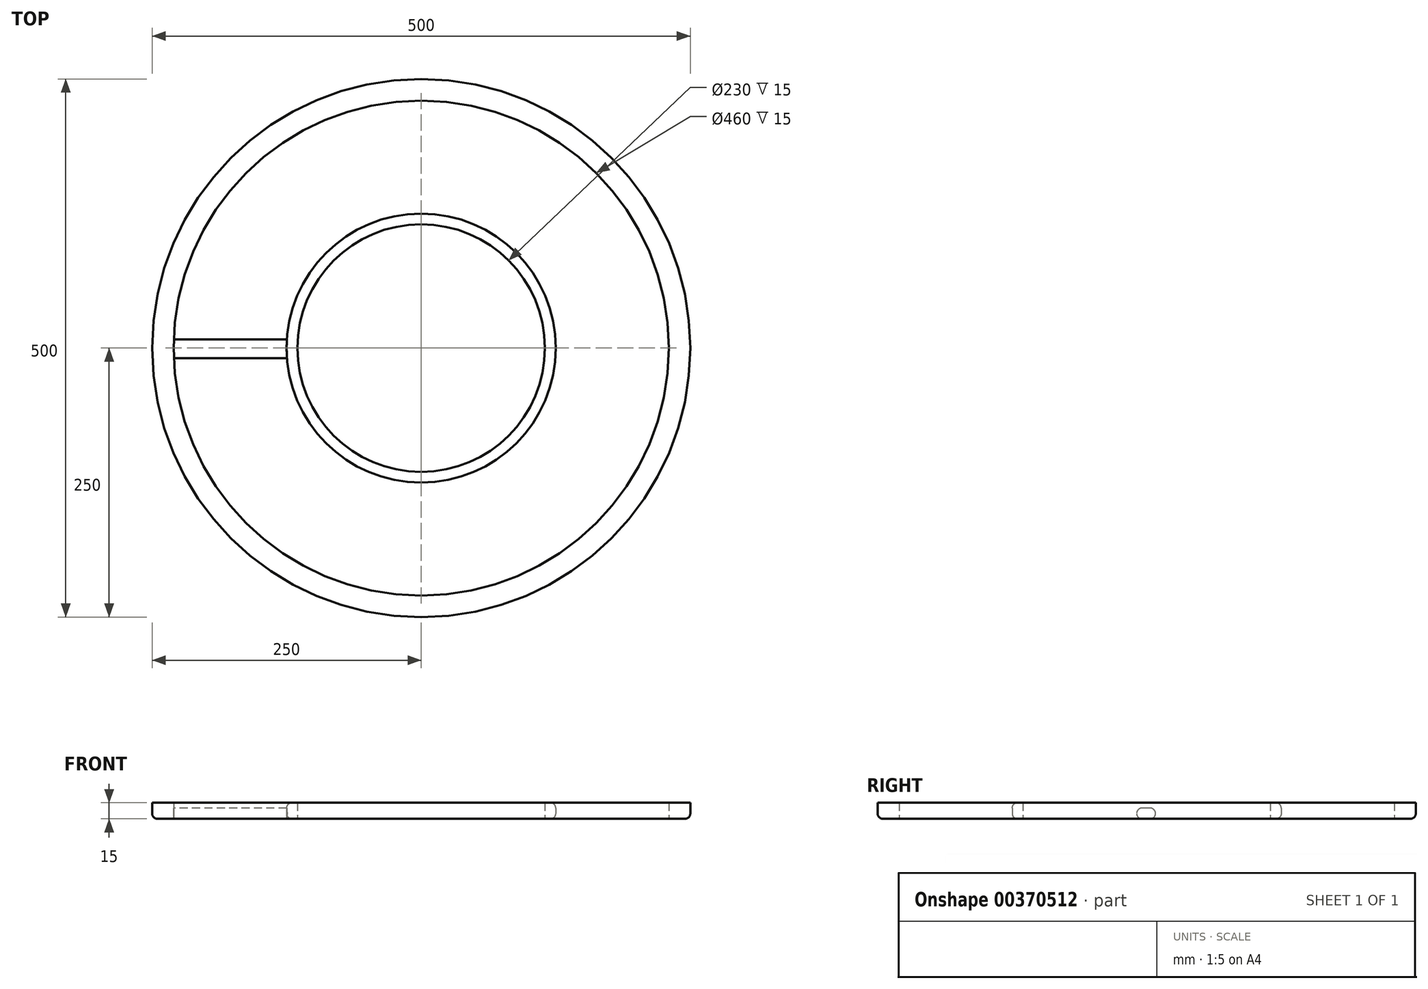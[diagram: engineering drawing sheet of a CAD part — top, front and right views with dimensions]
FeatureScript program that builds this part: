
annotation { "Feature Type Name" : "Feature", "Feature Type Description" : "" }
export const myFeature = defineFeature(function(context is Context, id is Id, definition is map)
    precondition{}
    {
        {
            var Q0;
            Q0=qCreatedBy(makeId("Top.planeOp"),FACE);
            var sketch = newSketch(context, id + "F0", { "sketchPlane" : qUnion([Q0])});
            skCircle(sketch, "E0", {"center": v(0, 0) * mm, "radius": 125 * mm});
            skCircle(sketch, "E1.0", {"center": v(0, 0) * mm, "radius": 115 * mm});
            skCircle(sketch, "E2", {"center": v(0, 0) * mm, "radius": 250 * mm});
            skCircle(sketch, "E3.0", {"center": v(0, 0) * mm, "radius": 230 * mm});
            skLineSegment(sketch, "E4.bottom", {"start": v(-124.73, 8.16) * mm, "end": v(-229.86, 8.16) * mm});
            skLineSegment(sketch, "E4.top", {"start": v(-124.65, -9.33) * mm, "end": v(-229.81, -9.33) * mm});
            skPoint(sketch, "E4.left.start.orphan", {"position": v(0, 8.16) * mm});
            skSolve(sketch);
        }
        {
            var Q0;
            Q0=makeQuery(id+"F0.imprint","IMPRINT",FACE,{"disambiguationData":[TD([[makeQuery(id+"F0.imprint","IMPRINT",EDGE,{"derivedFrom":sQuery(id+"F0.wireOp",EDGE,"E2")}),1.0]])]});
            var Q1;
            Q1=makeQuery(id+"F0.imprint","IMPRINT",FACE,{"disambiguationData":[TD([[makeQuery(id+"F0.imprint","IMPRINT",EDGE,{"derivedFrom":sQuery(id+"F0.wireOp",EDGE,"E0")}),1.0]])]});
            extrude(context, id + "F1", {"entities" : qUnion([Q0, Q1]), "depth" : 15 * mm});
        }
        {
            var Q0;
            {var subQ0=sQuery(id+"F0.wireOp",EDGE,"E4.bottom");Q0=makeQuery(id+"F0.imprint","IMPRINT",FACE,{"disambiguationData":[TD([[makeQuery(id+"F0.imprint","IMPRINT",EDGE,{"derivedFrom":subQ0}),1.0]])]});}
            extrude(context, id + "F2", {"entities" : qUnion([Q0]), "depth" : 10 * mm});
        }
        {
            var Q0;
            Q0=makeQuery(id+"F2.opExtrude","CAP_EDGE",EDGE,{"disambiguationData":[OSD([sQuery(id+"F0.wireOp",EDGE,"E4.bottom")])],"isStart":true});
            var Q1;
            Q1=makeQuery(id+"F2.opExtrude","CAP_EDGE",EDGE,{"disambiguationData":[OSD([sQuery(id+"F0.wireOp",EDGE,"E4.top")])],"isStart":true});
            var Q2;
            Q2=makeQuery(id+"F1.opExtrude","CAP_EDGE",EDGE,{"disambiguationData":[OSD([sQuery(id+"F0.wireOp",EDGE,"E2")])],"isStart":true});
            var Q3;
            Q3=makeQuery(id+"F1.opExtrude","CAP_EDGE",EDGE,{"disambiguationData":[OSD([sQuery(id+"F0.wireOp",EDGE,"E0")])],"isStart":true});
            var Q4;
            Q4=makeQuery(id+"F1.opExtrude","CAP_EDGE",EDGE,{"disambiguationData":[OSD([sQuery(id+"F0.wireOp",EDGE,"E0")])],"isStart":false});
            var Q5;
            Q5=makeQuery(id+"F2.opExtrude","CAP_EDGE",EDGE,{"disambiguationData":[OSD([sQuery(id+"F0.wireOp",EDGE,"E4.bottom")])],"isStart":false});
            var Q6;
            Q6=makeQuery(id+"F2.opExtrude","CAP_EDGE",EDGE,{"disambiguationData":[OSD([sQuery(id+"F0.wireOp",EDGE,"E4.top")])],"isStart":false});
            fillet(context, id + "F3", {"entities" : qUnion([Q0, Q1, Q2, Q3, Q4, Q5, Q6]), "radius" : 5 * mm, "tangentPropagation" : true, "allowEdgeOverflow" : false});
        }
    });
